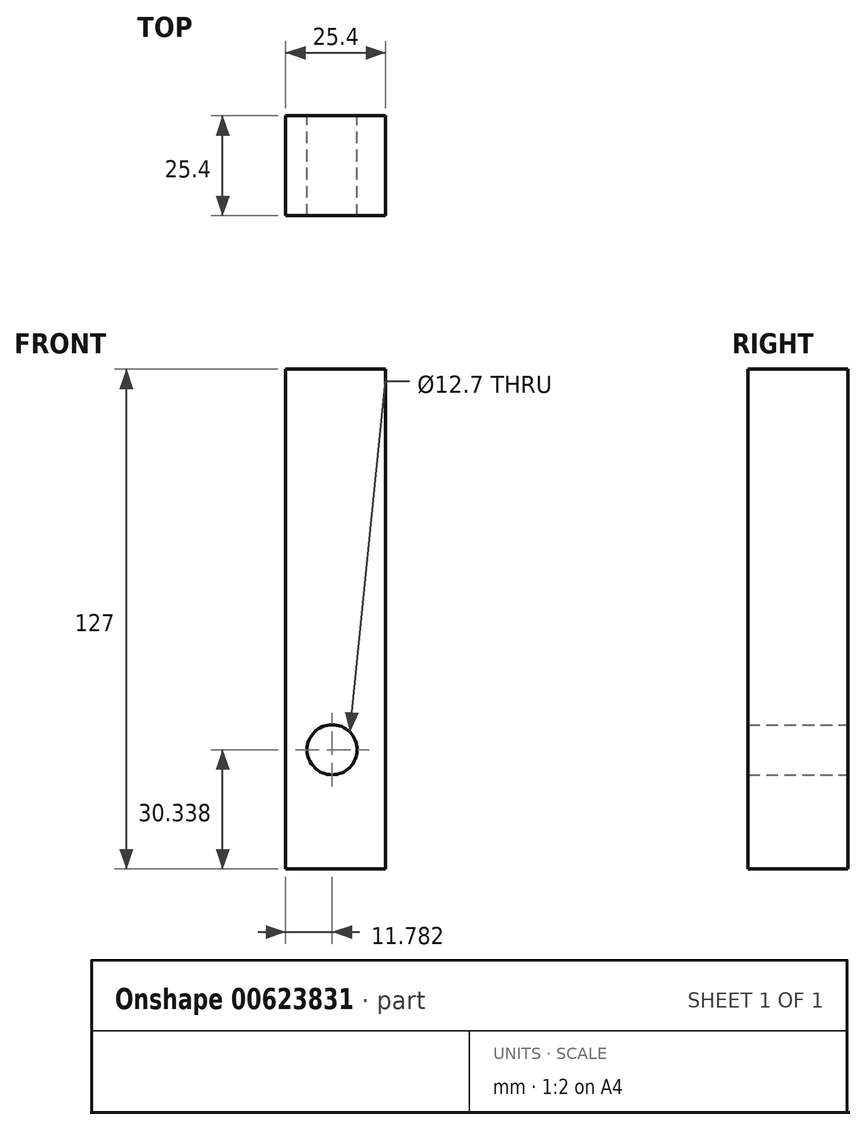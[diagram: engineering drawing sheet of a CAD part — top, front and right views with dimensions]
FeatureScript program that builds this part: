
annotation { "Feature Type Name" : "Feature", "Feature Type Description" : "" }
export const myFeature = defineFeature(function(context is Context, id is Id, definition is map)
    precondition{}
    {
        {
            var Q0;
            Q0=qCreatedBy(makeId("Front.planeOp"),FACE);
            var sketch = newSketch(context, id + "F0", { "sketchPlane" : qUnion([Q0])});
            skLineSegment(sketch, "E0.bottom", {"start": v(-48.58, 60.78) * mm, "end": v(-23.18, 60.78) * mm});
            skLineSegment(sketch, "E0.top", {"start": v(-48.58, -66.22) * mm, "end": v(-23.18, -66.22) * mm});
            skLineSegment(sketch, "E0.left", {"start": v(-48.58, 60.78) * mm, "end": v(-48.58, -66.22) * mm});
            skLineSegment(sketch, "E0.right", {"start": v(-23.18, 60.78) * mm, "end": v(-23.18, -66.22) * mm});
            skCircle(sketch, "E1", {"center": v(-36.8, -35.88) * mm, "radius": 6.35 * mm});
            skSolve(sketch);
        }
        {
            var Q0;
            Q0=makeQuery(id+"F0.imprint","IMPRINT",FACE,{"disambiguationData":[TD([[makeQuery(id+"F0.imprint","IMPRINT",EDGE,{"derivedFrom":sQuery(id+"F0.wireOp",EDGE,"E0.bottom")}),-1.0]])]});
            extrude(context, id + "F1", {"entities" : qUnion([Q0]), "depth" : 25.4 * mm, "offsetDistance" : 25.4 * mm});
        }
    });
